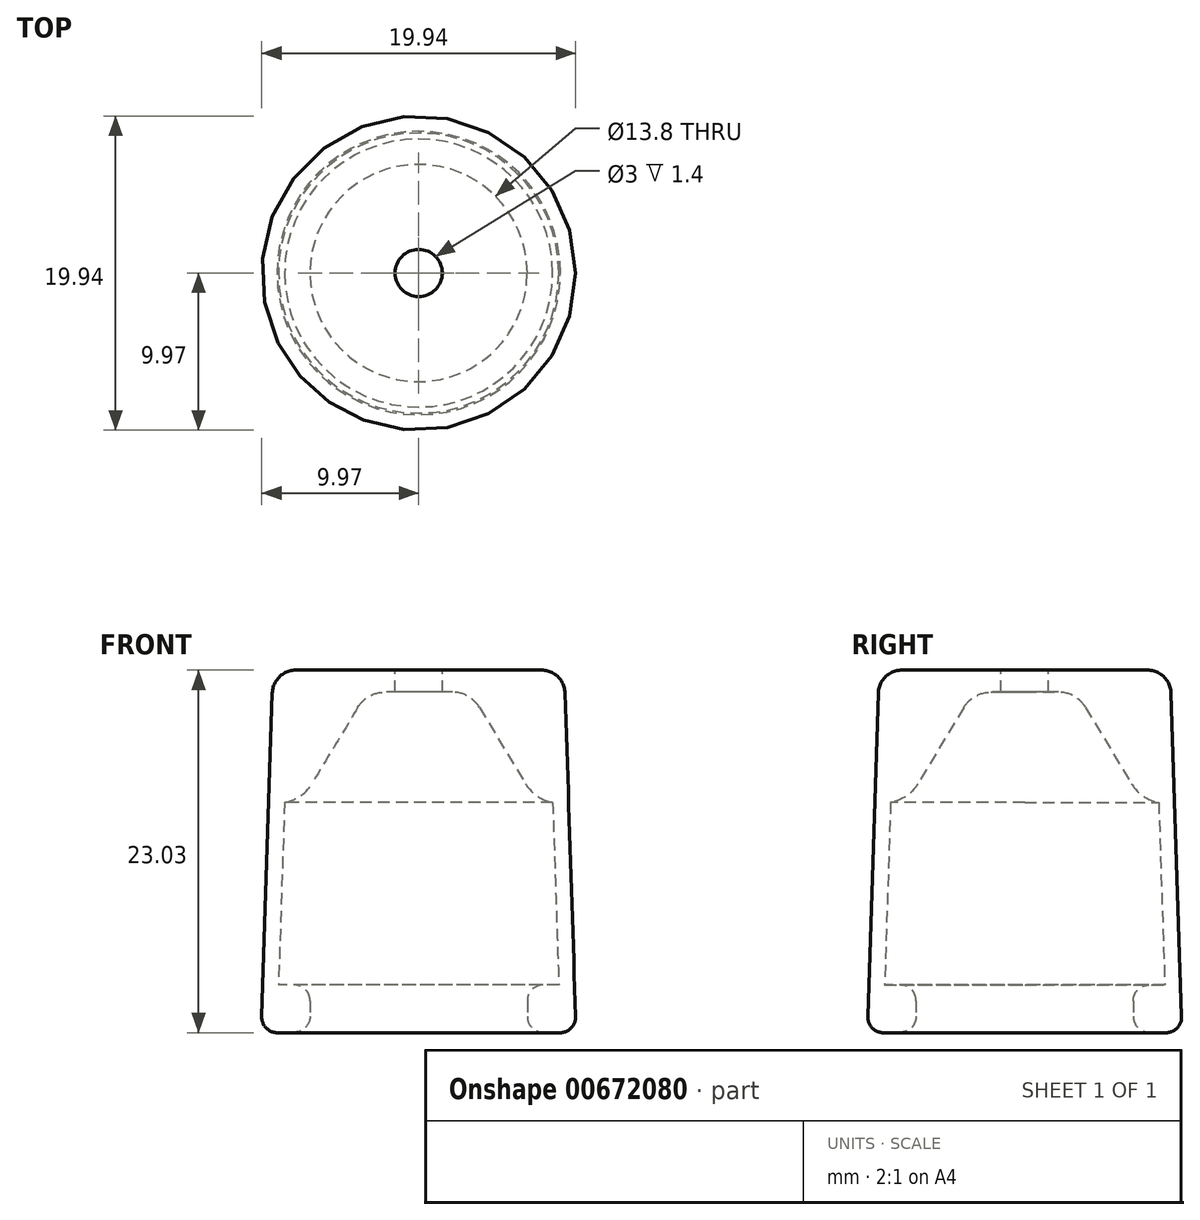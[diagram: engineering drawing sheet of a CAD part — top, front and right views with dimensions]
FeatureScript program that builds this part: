
annotation { "Feature Type Name" : "Feature", "Feature Type Description" : "" }
export const myFeature = defineFeature(function(context is Context, id is Id, definition is map)
    precondition{}
    {
        {
            var Q0;
            Q0=qCreatedBy(makeId("Front.planeOp"),FACE);
            var sketch = newSketch(context, id + "F0", { "sketchPlane" : qUnion([Q0])});
            skLineSegment(sketch, "E0", {"start": v(0, 23) * mm, "end": v(-9.25, 23) * mm});
            skLineSegment(sketch, "E1", {"start": v(-9.25, 23) * mm, "end": v(-10, 0) * mm});
            skLineSegment(sketch, "E2.0", {"start": v(-8.28, 21.6) * mm, "end": v(-9, -0.03) * mm});
            skLineSegment(sketch, "E2.1", {"start": v(0, 21.6) * mm, "end": v(-8.28, 21.6) * mm});
            skLineSegment(sketch, "E3", {"start": v(-10, 0) * mm, "end": v(-9, -0.03) * mm});
            skLineSegment(sketch, "E4", {"start": v(0, 31.13) * mm, "end": v(0, -6) * mm, "construction": true});
            skLineSegment(sketch, "E5", {"start": v(0, 23) * mm, "end": v(0, 21.6) * mm});
            skLineSegment(sketch, "E6", {"start": v(-8.28, 21.6) * mm, "end": v(-8.51, 14.6) * mm});
            skLineSegment(sketch, "E7", {"start": v(-8.51, 14.6) * mm, "end": v(-7.51, 14.57) * mm});
            skLineSegment(sketch, "E8", {"start": v(-7.51, 14.57) * mm, "end": v(-3.28, 21.6) * mm});
            skLineSegment(sketch, "E9", {"start": v(-3.28, 21.6) * mm, "end": v(-8.28, 21.6) * mm});
            skSolve(sketch);
        }
        {
            var Q0;
            Q0=qCreatedBy(makeId("Top.planeOp"),FACE);
            var sketch = newSketch(context, id + "F1", { "sketchPlane" : qUnion([Q0])});
            skCircle(sketch, "E10", {"center": v(0, 0) * mm, "radius": 9 * mm});
            skCircle(sketch, "E11", {"center": v(0, 0) * mm, "radius": 6.9 * mm});
            skSolve(sketch);
        }
        {
            var Q0;
            Q0=qSketchRegion(id+"F0",true);
            var Q1;
            Q1=sQuery(id+"F0.wireOp",EDGE,"E4");
            revolve(context, id + "F2", {"entities" : qUnion([Q0]), "axis" : qUnion([Q1]), "revolveType" : RevolveType.FULL});
        }
        {
            var Q0;
            Q0=qSketchRegion(id+"F0",true);
            var Q1;
            Q1=sQuery(id+"F0.wireOp",EDGE,"E4");
            revolve(context, id + "F3", {"operationType" : NewBodyOperationType.ADD, "entities" : qUnion([Q0]), "axis" : qUnion([Q1]), "revolveType" : RevolveType.FULL});
        }
        {
            var Q0;
            Q0=qSketchRegion(id+"F1",true);
            extrude(context, id + "F4", {"entities" : qUnion([Q0]), "operationType" : NewBodyOperationType.ADD, "depth" : 3 * mm, "offsetDistance" : 25 * mm});
        }
        {
            var Q0;
            Q0=qCreatedBy(makeId("Top.planeOp"),FACE);
            cPlane(context, id + "F5", {"entities" : qUnion([Q0]), "cplaneType" : CPlaneType.OFFSET, "offset" : 23 * mm, "width" : 150 * mm, "height" : 150 * mm});
        }
        {
            var Q0;
            Q0=qCreatedBy(id+"F5.planeOp",FACE);
            var sketch = newSketch(context, id + "F6", { "sketchPlane" : qUnion([Q0])});
            skPoint(sketch, "E12", {"position": v(0, 0) * mm});
            skSolve(sketch);
        }
        {
            var Q0;
            Q0=sQuery(id+"F6.wireOp",VERTEX,"E12");
            var Q1;
            Q1=makeQuery(id+"F2.opRevolve","SWEPT_BODY",BODY,{"disambiguationData":[OSD([sQuery(id+"F0.wireOp",EDGE,"E0"),sQuery(id+"F0.wireOp",EDGE,"E1"),sQuery(id+"F0.wireOp",EDGE,"E2.0"),sQuery(id+"F0.wireOp",EDGE,"E2.1"),sQuery(id+"F0.wireOp",EDGE,"E3"),sQuery(id+"F0.wireOp",EDGE,"E5")])]});
            hole(context, id + "F7", {"style" : HoleStyle.SIMPLE, "endStyle" : HoleEndStyle.BLIND, "holeDiameter" : 3 * mm, "majorDiameter" : 5 * mm, "holeDepth" : 12 * mm, "isTappedThrough" : true, "tappedDepth" : 12 * mm, "tapClearance" : 3, "startFromSketch" : true, "locations" : qUnion([Q0]), "scope" : qUnion([Q1])});
        }
        {
            var Q0;
            Q0=makeQuery(id+"F2.opRevolve","SWEPT_EDGE",EDGE,{"disambiguationData":[OSD([sQuery(id+"F0.wireOp",EDGE,"E0"),sQuery(id+"F0.wireOp",EDGE,"E1")])]});
            fillet(context, id + "F8", {"entities" : qUnion([Q0]), "radius" : 1.5 * mm, "tangentPropagation" : true, "allowEdgeOverflow" : false});
        }
        {
            var Q0;
            Q0=makeQuery(id+"F2.opRevolve","SWEPT_EDGE",EDGE,{"disambiguationData":[OSD([sQuery(id+"F0.wireOp",EDGE,"E1"),sQuery(id+"F0.wireOp",EDGE,"E3")])]});
            var Q1;
            Q1=makeQuery(id+"F4.opExtrude","CAP_EDGE",EDGE,{"disambiguationData":[OSD([sQuery(id+"F1.wireOp",EDGE,"E11")])],"isStart":true});
            var Q2;
            Q2=makeQuery(id+"F4.opExtrude","CAP_EDGE",EDGE,{"disambiguationData":[OSD([sQuery(id+"F1.wireOp",EDGE,"E11")])],"isStart":false});
            fillet(context, id + "F9", {"entities" : qUnion([Q0, Q1, Q2]), "radius" : 1 * mm, "tangentPropagation" : true, "allowEdgeOverflow" : false});
        }
        {
            var Q0;
            Q0=makeQuery(id+"F2.opRevolve","SWEPT_EDGE",EDGE,{"disambiguationData":[OSD([sQuery(id+"F0.wireOp",EDGE,"E7"),sQuery(id+"F0.wireOp",EDGE,"E8")])]});
            fillet(context, id + "F10", {"entities" : qUnion([Q0]), "radius" : 2.5 * mm, "tangentPropagation" : true, "allowEdgeOverflow" : false});
        }
        {
            var Q0;
            Q0=makeQuery(id+"F2.opRevolve","SWEPT_EDGE",EDGE,{"disambiguationData":[OSD([sQuery(id+"F0.wireOp",EDGE,"E2.1"),sQuery(id+"F0.wireOp",EDGE,"E8"),sQuery(id+"F0.wireOp",EDGE,"E9")])]});
            fillet(context, id + "F11", {"entities" : qUnion([Q0]), "radius" : 2 * mm, "tangentPropagation" : true, "allowEdgeOverflow" : false});
        }
    });
